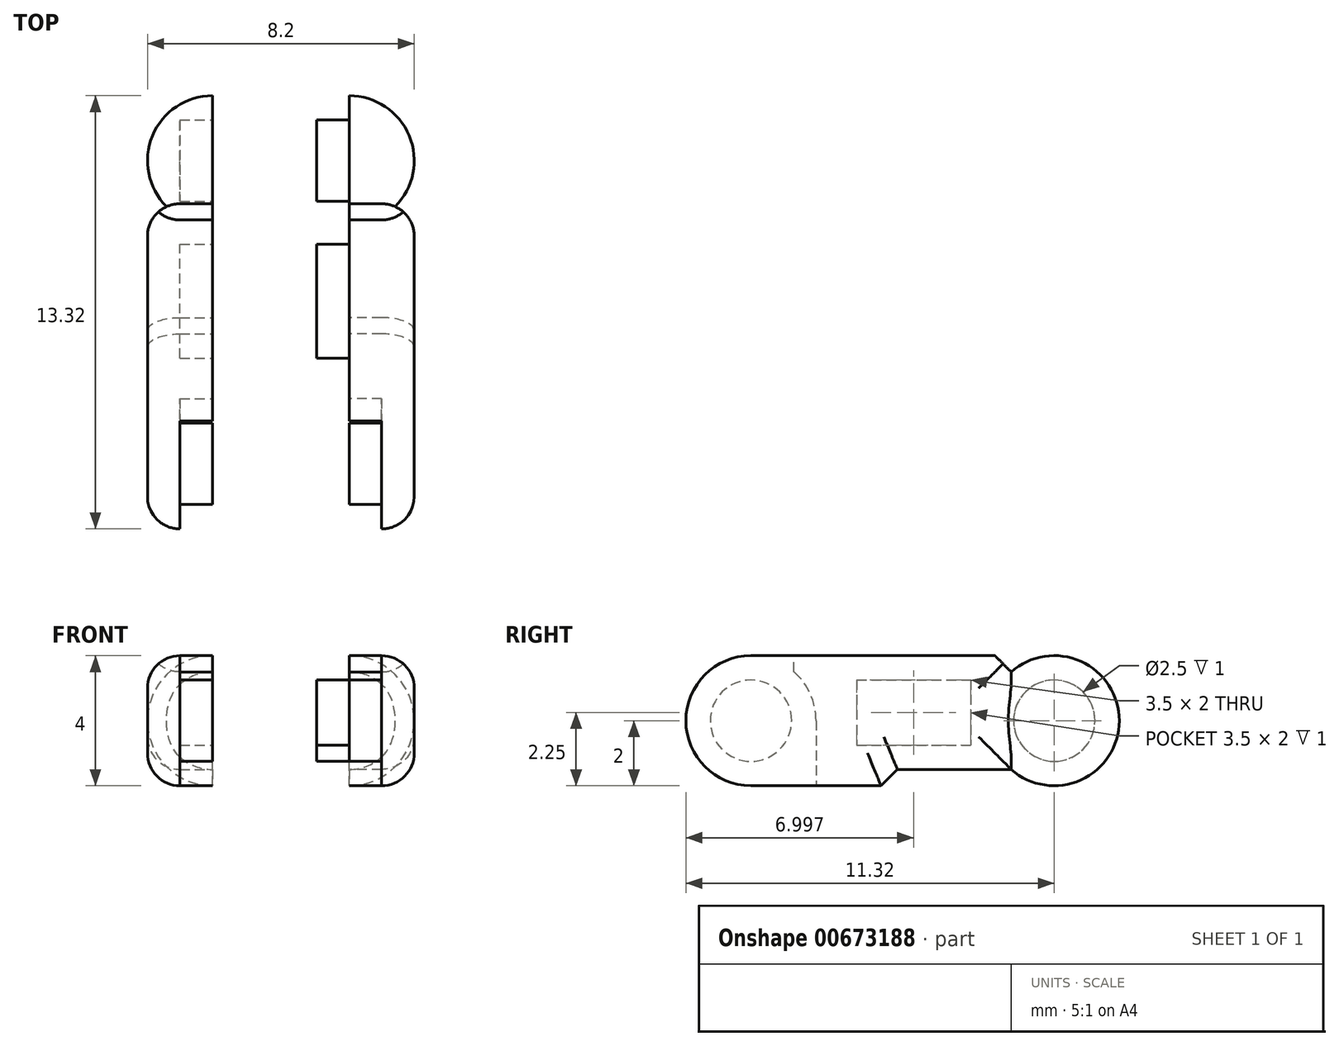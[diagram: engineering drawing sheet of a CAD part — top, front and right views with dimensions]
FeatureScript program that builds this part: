
annotation { "Feature Type Name" : "Feature", "Feature Type Description" : "" }
export const myFeature = defineFeature(function(context is Context, id is Id, definition is map)
    precondition{}
    {
        {
            var Q0;
            Q0=qCreatedBy(makeId("Right.planeOp"),FACE);
            var sketch = newSketch(context, id + "F0", { "sketchPlane" : qUnion([Q0])});
            skArc(sketch, "E0", {"start": v(-1.32, -1.5) * mm, "mid": v(0.82, -1.82) * mm, "end": v(2, 0) * mm});
            skLineSegment(sketch, "E1", {"start": v(-1.32, 1.5) * mm, "end": v(-9.32, 1.5) * mm});
            skLineSegment(sketch, "E2", {"start": v(-9.32, 1.5) * mm, "end": v(-9.32, -1.5) * mm});
            skLineSegment(sketch, "E3", {"start": v(-9.32, -1.5) * mm, "end": v(-1.32, -1.5) * mm});
            skPoint(sketch, "E4.orphan", {"position": v(0, -1.5) * mm});
            skLineSegment(sketch, "E5", {"start": v(-1.32, 1.5) * mm, "end": v(-1.32, -1.5) * mm});
            skCircle(sketch, "E6", {"center": v(-9.32, 0) * mm, "radius": 2 * mm});
            skLineSegment(sketch, "E7", {"start": v(-9.32, 2) * mm, "end": v(-1.82, 2) * mm});
            skLineSegment(sketch, "E8", {"start": v(-1.32, 1.5) * mm, "end": v(-1.82, 2) * mm});
            skPoint(sketch, "E9.orphan", {"position": v(-1.32, 2) * mm});
            skLineSegment(sketch, "E10", {"start": v(-9.32, -2) * mm, "end": v(-5.32, -2) * mm});
            skPoint(sketch, "E10.endSnap0", {"position": v(-5.32, -1.5) * mm});
            skLineSegment(sketch, "E11", {"start": v(-5.32, -2) * mm, "end": v(-4.82, -1.5) * mm});
            skLineSegment(sketch, "E12", {"start": v(2, 0) * mm, "end": v(-1.32, 0) * mm});
            skLineSegment(sketch, "E13", {"start": v(-7.32, 0) * mm, "end": v(-7.32, -2) * mm});
            skLineSegment(sketch, "E14", {"start": v(-8, 1.5) * mm, "end": v(-8, 2) * mm});
            skSolve(sketch);
        }
        {
            var Q0;
            {var subQ4=sQuery(id+"F0.wireOp",EDGE,"E7");Q0=makeQuery(id+"F0.imprint","IMPRINT",FACE,{"disambiguationData":[TD([[makeQuery(id+"F0.imprint","IMPRINT",EDGE,{"derivedFrom":subQ4}),-1.0]])]});}
            var Q1;
            {var subQ4=sQuery(id+"F0.wireOp",EDGE,"E10");Q1=makeQuery(id+"F0.imprint","IMPRINT",FACE,{"disambiguationData":[TD([[makeQuery(id+"F0.imprint","IMPRINT",EDGE,{"derivedFrom":subQ4}),1.0]])]});}
            var Q2;
            {var subQ1=sQuery(id+"F0.wireOp",EDGE,"E2");Q2=makeQuery(id+"F0.imprint","IMPRINT",FACE,{"disambiguationData":[TD([[makeQuery(id+"F0.imprint","IMPRINT",EDGE,{"derivedFrom":subQ1}),-1.0]])]});}
            var Q3;
            {var subQ0=sQuery(id+"F0.wireOp",EDGE,"E3");var subQ1=makeQuery(id+"F0.imprint","INTERSECT",VERTEX,{"derivedFrom":[subQ0,sQuery(id+"F0.wireOp",EDGE,"E11")]});Q3=makeQuery(id+"F0.imprint","IMPRINT",FACE,{"disambiguationData":[TD([[makeQuery(id+"F0.imprint","IMPRINT",EDGE,{"disambiguationData":[TD([[subQ1,1.0]])],"derivedFrom":subQ0}),1.0]])]});}
            var Q4;
            {var subQ0=sQuery(id+"F0.wireOp",EDGE,"E2");Q4=makeQuery(id+"F0.imprint","IMPRINT",FACE,{"disambiguationData":[TD([[makeQuery(id+"F0.imprint","IMPRINT",EDGE,{"derivedFrom":subQ0}),1.0]])]});}
            var Q5;
            {var subQ0=sQuery(id+"F0.wireOp",EDGE,"E5");Q5=makeQuery(id+"F0.imprint","IMPRINT",FACE,{"disambiguationData":[TD([[makeQuery(id+"F0.imprint","IMPRINT",EDGE,{"derivedFrom":subQ0}),-1.0]])]});}
            var Q6;
            {var subQ0=sQuery(id+"F0.wireOp",EDGE,"E8");Q6=makeQuery(id+"F0.imprint","IMPRINT",FACE,{"disambiguationData":[TD([[makeQuery(id+"F0.imprint","IMPRINT",EDGE,{"derivedFrom":subQ0}),1.0]])]});}
            var Q7;
            {var subQ0=sQuery(id+"F0.wireOp",EDGE,"E6");var subQ1=sQuery(id+"F0.wireOp",EDGE,"E3");var subQ2=makeQuery(id+"F0.imprint","INTERSECT",VERTEX,{"derivedFrom":[subQ1,subQ0]});Q7=makeQuery(id+"F0.imprint","IMPRINT",FACE,{"disambiguationData":[TD([[makeQuery(id+"F0.imprint","IMPRINT",EDGE,{"disambiguationData":[TD([[subQ2,-1.0]])],"derivedFrom":subQ1}),1.0]])]});}
            extrude(context, id + "F1", {"entities" : qUnion([Q0, Q1, Q2, Q3, Q4, Q5, Q6, Q7]), "oppositeDirection" : true, "depth" : 2 * mm});
        }
        {
            var Q0;
            {var subQ0=sQuery(id+"F0.wireOp",EDGE,"E0");Q0=makeQuery(id+"F0.imprint","IMPRINT",FACE,{"disambiguationData":[TD([[makeQuery(id+"F0.imprint","IMPRINT",EDGE,{"derivedFrom":subQ0}),1.0]])]});}
            var Q1;
            Q1=sQuery(id+"F0.wireOp",EDGE,"E12");
            revolve(context, id + "F2", {"operationType" : NewBodyOperationType.ADD, "entities" : qUnion([Q0]), "axis" : qUnion([Q1]), "revolveType" : RevolveType.FULL});
        }
        {
            var Q0;
            Q0=makeQuery(id+"F2.opRevolve","SWEPT_FACE",FACE,{"disambiguationData":[OSD([sQuery(id+"F0.wireOp",EDGE,"E5")])]});
            var sketch = newSketch(context, id + "F3", { "sketchPlane" : qUnion([Q0])});
            skLineSegment(sketch, "E15.bottom", {"start": v(0, -2.8) * mm, "end": v(3.04, -2.8) * mm});
            skLineSegment(sketch, "E15.top", {"start": v(0, 2.5) * mm, "end": v(3.04, 2.5) * mm});
            skLineSegment(sketch, "E15.left", {"start": v(0, -2.8) * mm, "end": v(0, 2.5) * mm});
            skLineSegment(sketch, "E15.right", {"start": v(3.04, -2.8) * mm, "end": v(3.04, 2.5) * mm});
            skSolve(sketch);
        }
        {
            var Q0;
            Q0=qSketchRegion(id+"F3",true);
            extrude(context, id + "F4", {"entities" : qUnion([Q0]), "operationType" : NewBodyOperationType.REMOVE, "oppositeDirection" : true, "depth" : 25 * mm});
        }
        {
            var Q0;
            Q0=makeQuery(id+"F1.opExtrude","CAP_FACE",FACE,{"disambiguationData":[OSD([sQuery(id+"F0.wireOp",EDGE,"E3"),sQuery(id+"F0.wireOp",EDGE,"E5"),sQuery(id+"F0.wireOp",EDGE,"E6"),sQuery(id+"F0.wireOp",EDGE,"E7"),sQuery(id+"F0.wireOp",EDGE,"E8"),sQuery(id+"F0.wireOp",EDGE,"E10"),sQuery(id+"F0.wireOp",EDGE,"E11")])],"isStart":false});
            fillet(context, id + "F5", {"entities" : qUnion([Q0]), "radius" : 1 * mm, "tangentPropagation" : true, "allowEdgeOverflow" : false});
        }
        {
            var Q0;
            {var subQ5=sQuery(id+"F0.wireOp",EDGE,"E2");Q0=makeQuery(id+"F0.imprint","IMPRINT",FACE,{"disambiguationData":[TD([[makeQuery(id+"F0.imprint","IMPRINT",EDGE,{"derivedFrom":subQ5}),-1.0]])]});}
            var Q1;
            {var subQ3=sQuery(id+"F0.wireOp",EDGE,"E14");Q1=makeQuery(id+"F0.imprint","IMPRINT",FACE,{"disambiguationData":[TD([[makeQuery(id+"F0.imprint","IMPRINT",EDGE,{"derivedFrom":subQ3}),1.0]])]});}
            var Q2;
            {var subQ5=sQuery(id+"F0.wireOp",EDGE,"E2");Q2=makeQuery(id+"F0.imprint","IMPRINT",FACE,{"disambiguationData":[TD([[makeQuery(id+"F0.imprint","IMPRINT",EDGE,{"derivedFrom":subQ5}),1.0]])]});}
            var Q3;
            {var subQ0=sQuery(id+"F0.wireOp",EDGE,"E6");var subQ1=sQuery(id+"F0.wireOp",EDGE,"E3");var subQ2=makeQuery(id+"F0.imprint","INTERSECT",VERTEX,{"derivedFrom":[subQ1,subQ0]});Q3=makeQuery(id+"F0.imprint","IMPRINT",FACE,{"disambiguationData":[TD([[makeQuery(id+"F0.imprint","IMPRINT",EDGE,{"disambiguationData":[TD([[subQ2,-1.0]])],"derivedFrom":subQ1}),1.0]])]});}
            var Q4;
            {var subQ0=sQuery(id+"F0.wireOp",EDGE,"E6");var subQ1=sQuery(id+"F0.wireOp",EDGE,"E3");var subQ2=makeQuery(id+"F0.imprint","INTERSECT",VERTEX,{"derivedFrom":[subQ1,subQ0]});Q4=makeQuery(id+"F0.imprint","IMPRINT",FACE,{"disambiguationData":[TD([[makeQuery(id+"F0.imprint","IMPRINT",EDGE,{"disambiguationData":[TD([[subQ2,-1.0]])],"derivedFrom":subQ1}),-1.0]])]});}
            extrude(context, id + "F6", {"entities" : qUnion([Q0, Q1, Q2, Q3, Q4]), "operationType" : NewBodyOperationType.REMOVE, "oppositeDirection" : true, "depth" : 1 * mm});
        }
        {
            var Q0;
            Q0=makeQuery(id+"F6.boolean.opBoolean","COPY",FACE,{"derivedFrom":makeQuery(id+"F6.opExtrude","CAP_FACE",FACE,{"disambiguationData":[OSD([sQuery(id+"F0.wireOp",EDGE,"E6"),sQuery(id+"F0.wireOp",EDGE,"E7"),sQuery(id+"F0.wireOp",EDGE,"E10"),sQuery(id+"F0.wireOp",EDGE,"E13"),sQuery(id+"F0.wireOp",EDGE,"E14")])],"isStart":false})});
            var sketch = newSketch(context, id + "F7", { "sketchPlane" : qUnion([Q0])});
            skCircle(sketch, "E16", {"center": v(-9.32, 0) * mm, "radius": 1.25 * mm});
            skSolve(sketch);
        }
        {
            var Q0;
            Q0=qSketchRegion(id+"F7",true);
            extrude(context, id + "F8", {"entities" : qUnion([Q0]), "operationType" : NewBodyOperationType.ADD, "depth" : 1 * mm});
        }
        {
            var Q0;
            Q0=makeQuery(id+"F4.boolean.opBoolean","MERGE",FACE,{"derivedFrom":[makeQuery(id+"F1.opExtrude","CAP_FACE",FACE,{"disambiguationData":[OSD([sQuery(id+"F0.wireOp",EDGE,"E3"),sQuery(id+"F0.wireOp",EDGE,"E5"),sQuery(id+"F0.wireOp",EDGE,"E6"),sQuery(id+"F0.wireOp",EDGE,"E7"),sQuery(id+"F0.wireOp",EDGE,"E8"),sQuery(id+"F0.wireOp",EDGE,"E10"),sQuery(id+"F0.wireOp",EDGE,"E11")])],"isStart":true}),makeQuery(id+"F4.opExtrude","SWEPT_FACE",FACE,{"disambiguationData":[OSD([sQuery(id+"F3.wireOp",EDGE,"E15.left")])]})]});
            var sketch = newSketch(context, id + "F9", { "sketchPlane" : qUnion([Q0])});
            skLineSegment(sketch, "E17.bottom", {"start": v(-6.07, 1.25) * mm, "end": v(-2.57, 1.25) * mm});
            skLineSegment(sketch, "E17.top", {"start": v(-6.07, -0.75) * mm, "end": v(-2.57, -0.75) * mm});
            skLineSegment(sketch, "E17.left", {"start": v(-6.07, 1.25) * mm, "end": v(-6.07, -0.75) * mm});
            skLineSegment(sketch, "E17.right", {"start": v(-2.57, 1.25) * mm, "end": v(-2.57, -0.75) * mm});
            skCircle(sketch, "E18", {"center": v(0, 0) * mm, "radius": 1.25 * mm});
            skSolve(sketch);
        }
        {
            var Q0;
            Q0=qSketchRegion(id+"F9",true);
            extrude(context, id + "F10", {"entities" : qUnion([Q0]), "operationType" : NewBodyOperationType.REMOVE, "oppositeDirection" : true, "depth" : 1 * mm});
        }
        {
            var Q0;
            Q0=qCreatedBy(makeId("Right.planeOp"),FACE);
            cPlane(context, id + "F11", {"entities" : qUnion([Q0]), "cplaneType" : CPlaneType.OFFSET, "offset" : 2.1 * mm, "width" : 150 * mm, "height" : 150 * mm});
        }
        {
            var Q0;
            Q0=makeQuery(id+"F1.opExtrude","SWEPT_BODY",BODY,{"disambiguationData":[OSD([sQuery(id+"F0.wireOp",EDGE,"E3"),sQuery(id+"F0.wireOp",EDGE,"E5"),sQuery(id+"F0.wireOp",EDGE,"E6"),sQuery(id+"F0.wireOp",EDGE,"E7"),sQuery(id+"F0.wireOp",EDGE,"E8"),sQuery(id+"F0.wireOp",EDGE,"E10"),sQuery(id+"F0.wireOp",EDGE,"E11")])]});
            var Q1;
            Q1=qCreatedBy(id+"F11.planeOp",FACE);
            mirror(context, id + "F12", {"entities" : qUnion([Q0]), "mirrorPlane" : qUnion([Q1])});
        }
        {
            var Q0;
            Q0=makeQuery(id+"F12.opPattern","COPY",FACE,{"derivedFrom":makeQuery(id+"F10.boolean.opBoolean","COPY",FACE,{"derivedFrom":makeQuery(id+"F10.opExtrude","CAP_FACE",FACE,{"disambiguationData":[OSD([sQuery(id+"F9.wireOp",EDGE,"E17.bottom"),sQuery(id+"F9.wireOp",EDGE,"E17.top"),sQuery(id+"F9.wireOp",EDGE,"E17.left"),sQuery(id+"F9.wireOp",EDGE,"E17.right")])],"isStart":false})}),"instanceName":"1"});
            var Q1;
            Q1=makeQuery(id+"F12.opPattern","COPY",FACE,{"derivedFrom":makeQuery(id+"F10.boolean.opBoolean","COPY",FACE,{"derivedFrom":makeQuery(id+"F10.opExtrude","CAP_FACE",FACE,{"disambiguationData":[OSD([sQuery(id+"F9.wireOp",EDGE,"E18")])],"isStart":false})}),"instanceName":"1"});
            extrude(context, id + "F13", {"entities" : qUnion([Q0, Q1]), "operationType" : NewBodyOperationType.ADD, "depth" : 2 * mm});
        }
    });
